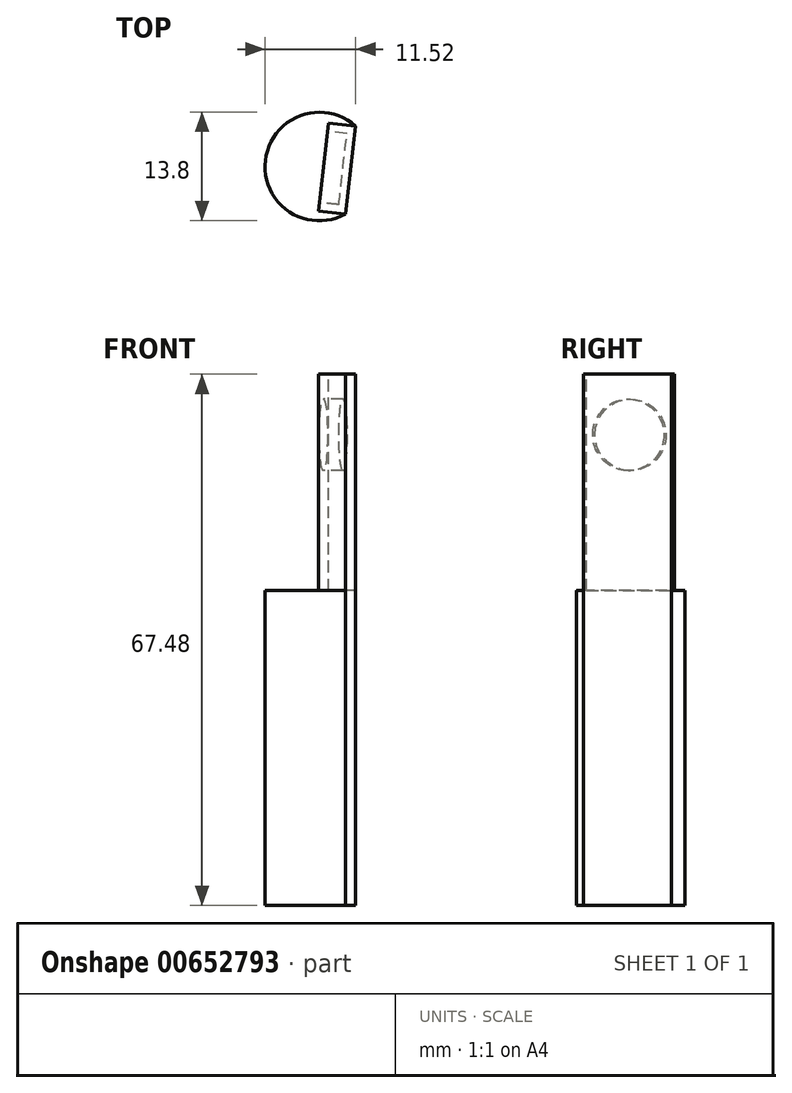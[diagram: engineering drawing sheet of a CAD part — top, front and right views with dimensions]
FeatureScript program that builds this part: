
annotation { "Feature Type Name" : "Feature", "Feature Type Description" : "" }
export const myFeature = defineFeature(function(context is Context, id is Id, definition is map)
    precondition{}
    {
        {
            var Q0;
            Q0=qCreatedBy(makeId("Top.planeOp"),FACE);
            var sketch = newSketch(context, id + "F0", { "sketchPlane" : qUnion([Q0])});
            skCircle(sketch, "E0", {"center": v(-26.37, 6.64) * mm, "radius": 6.9 * mm});
            skSolve(sketch);
        }
        {
            var Q0;
            Q0 = qSketchRegion(id + "F0", true);
            extrude(context, id + "F1", {"entities" : qUnion([Q0]), "depth" : 40 * mm, "offsetDistance" : 25 * mm});
        }
        {
            var Q0;
            Q0=makeQuery(id+"F1.opExtrude","CAP_FACE",FACE,{"disambiguationData":[OSD([sQuery(id+"F0.wireOp",EDGE,"E0")])],"isStart":true});
            var sketch = newSketch(context, id + "F2", { "sketchPlane" : qUnion([Q0])});
            skLineSegment(sketch, "E1", {"start": v(-23.01, -0.6) * mm, "end": v(-21.75, -11.76) * mm, "construction": true});
            skLineSegment(sketch, "E2", {"start": v(-23.01, -0.6) * mm, "end": v(-21.75, -11.76) * mm});
            skLineSegment(sketch, "E3", {"start": v(-16.14, -11.27) * mm, "end": v(-17.37, 0.4) * mm});
            skLineSegment(sketch, "E4", {"start": v(-17.37, 0.4) * mm, "end": v(-23.01, -0.6) * mm});
            skLineSegment(sketch, "E5", {"start": v(-16.14, -11.27) * mm, "end": v(-21.75, -11.76) * mm});
            skSolve(sketch);
        }
        {
            var Q0;
            Q0 = qSketchRegion(id + "F2", true);
            extrude(context, id + "F3", {"entities" : qUnion([Q0]), "operationType" : NewBodyOperationType.REMOVE, "oppositeDirection" : true, "depth" : 40 * mm, "offsetDistance" : 25 * mm});
        }
        {
            var Q0;
            Q0=makeQuery(id+"F3.boolean.opBoolean","COPY",FACE,{"derivedFrom":makeQuery(id+"F3.opExtrude","SWEPT_FACE",FACE,{"disambiguationData":[OSD([sQuery(id+"F2.wireOp",EDGE,"E2")])]})});
            var sketch = newSketch(context, id + "F4", { "sketchPlane" : qUnion([Q0])});
            skLineSegment(sketch, "E6.bottom", {"start": v(-1.99, 40) * mm, "end": v(9.24, 40) * mm});
            skLineSegment(sketch, "E6.top", {"start": v(-1.99, 50.52) * mm, "end": v(9.24, 50.52) * mm});
            skLineSegment(sketch, "E6.left", {"start": v(-1.99, 40) * mm, "end": v(-1.99, 50.52) * mm});
            skLineSegment(sketch, "E6.right", {"start": v(9.24, 40) * mm, "end": v(9.24, 50.52) * mm});
            skSolve(sketch);
        }
        {
            var Q0;
            Q0 = qSketchRegion(id + "F4", true);
            extrude(context, id + "F5", {"entities" : qUnion([Q0]), "operationType" : NewBodyOperationType.ADD, "depth" : -3.5 * mm, "offsetDistance" : 25 * mm});
        }
        {
            var Q0;
            Q0=makeQuery(id+"F5.boolean.opBoolean","MERGE",FACE,{"derivedFrom":[makeQuery(id+"F3.boolean.opBoolean","COPY",FACE,{"derivedFrom":makeQuery(id+"F3.opExtrude","SWEPT_FACE",FACE,{"disambiguationData":[OSD([sQuery(id+"F2.wireOp",EDGE,"E2")])]})}),makeQuery(id+"F5.opExtrude","CAP_FACE",FACE,{"disambiguationData":[OSD([sQuery(id+"F4.wireOp",EDGE,"E6.bottom"),sQuery(id+"F4.wireOp",EDGE,"E6.top"),sQuery(id+"F4.wireOp",EDGE,"E6.left"),sQuery(id+"F4.wireOp",EDGE,"E6.right")])],"isStart":true})]});
            var sketch = newSketch(context, id + "F6", { "sketchPlane" : qUnion([Q0])});
            skLineSegment(sketch, "E7.bottom", {"start": v(-1.99, 50.52) * mm, "end": v(9.24, 50.52) * mm});
            skLineSegment(sketch, "E7.top", {"start": v(-1.99, 67.48) * mm, "end": v(9.24, 67.48) * mm});
            skLineSegment(sketch, "E7.left", {"start": v(-1.99, 50.52) * mm, "end": v(-1.99, 67.48) * mm});
            skLineSegment(sketch, "E7.right", {"start": v(9.24, 50.52) * mm, "end": v(9.24, 67.48) * mm});
            skSolve(sketch);
        }
        {
            var Q0;
            Q0 = qSketchRegion(id + "F6", true);
            extrude(context, id + "F7", {"entities" : qUnion([Q0]), "operationType" : NewBodyOperationType.ADD, "depth" : -3.5 * mm, "offsetDistance" : 25 * mm});
        }
        {
            var Q0;
            Q0=makeQuery(id+"F7.boolean.opBoolean","MERGE",FACE,{"derivedFrom":[makeQuery(id+"F5.opExtrude","CAP_FACE",FACE,{"disambiguationData":[OSD([sQuery(id+"F4.wireOp",EDGE,"E6.bottom"),sQuery(id+"F4.wireOp",EDGE,"E6.top"),sQuery(id+"F4.wireOp",EDGE,"E6.left"),sQuery(id+"F4.wireOp",EDGE,"E6.right")])],"isStart":false}),makeQuery(id+"F7.opExtrude","CAP_FACE",FACE,{"disambiguationData":[OSD([sQuery(id+"F6.wireOp",EDGE,"E7.bottom"),sQuery(id+"F6.wireOp",EDGE,"E7.top"),sQuery(id+"F6.wireOp",EDGE,"E7.left"),sQuery(id+"F6.wireOp",EDGE,"E7.right")])],"isStart":false})]});
            var sketch = newSketch(context, id + "F8", { "sketchPlane" : qUnion([Q0])});
            skCircle(sketch, "E8", {"center": v(-3.64, 59.78) * mm, "radius": 4.55 * mm});
            skSolve(sketch);
        }
        {
            var Q0;
            Q0 = qSketchRegion(id + "F8", true);
            extrude(context, id + "F9", {"entities" : qUnion([Q0]), "operationType" : NewBodyOperationType.REMOVE, "oppositeDirection" : true, "depth" : 2.5 * mm, "offsetDistance" : 25 * mm});
        }
    });
